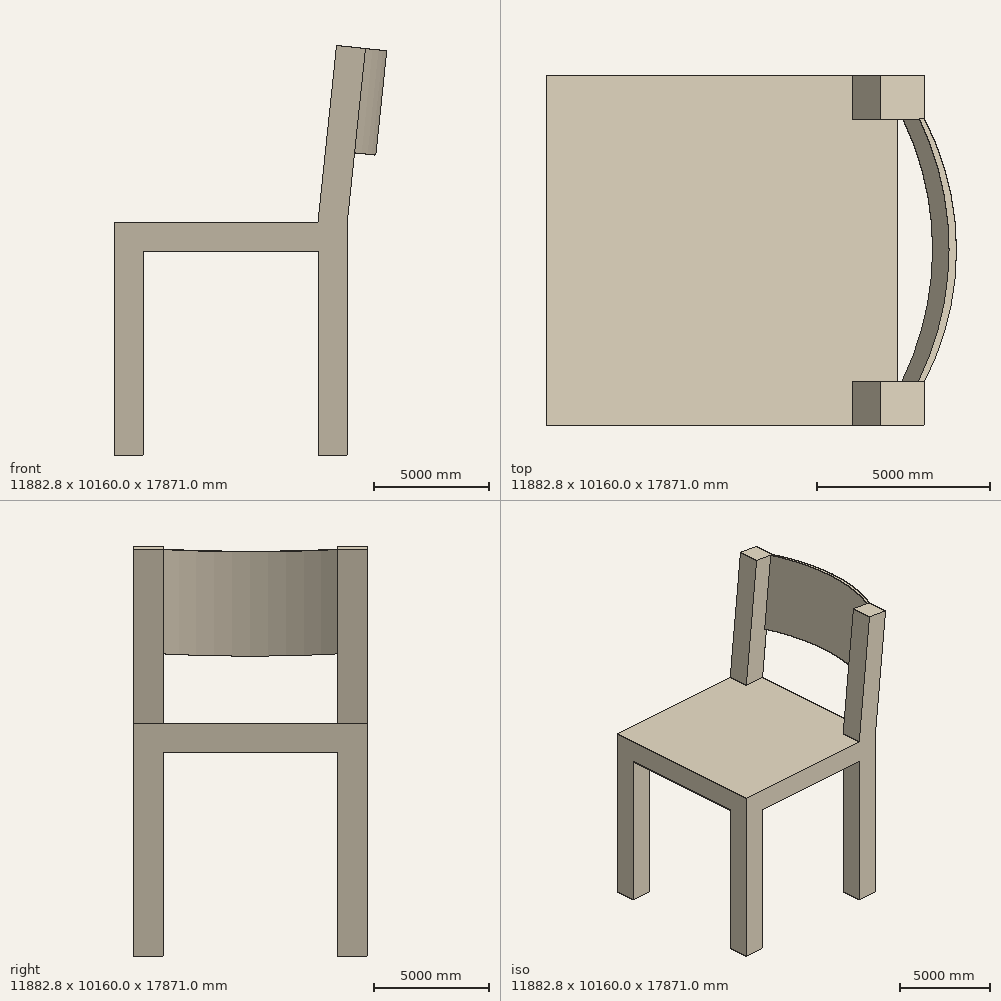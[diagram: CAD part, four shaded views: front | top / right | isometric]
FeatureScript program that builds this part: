
annotation { "Feature Type Name" : "Feature", "Feature Type Description" : "" }
export const myFeature = defineFeature(function(context is Context, id is Id, definition is map)
    precondition{}
    {
        {
            var Q0;
            Q0=qCreatedBy(makeId("Front.planeOp"),FACE);
            var sketch = newSketch(context, id + "F0", { "sketchPlane" : qUnion([Q0])});
            skLineSegment(sketch, "E0.bottom", {"start": v(-3222, -5083.92) * mm, "end": v(6938, -5083.92) * mm});
            skLineSegment(sketch, "E0.top", {"start": v(-3222, 5076.08) * mm, "end": v(6938, 5076.08) * mm});
            skLineSegment(sketch, "E0.left", {"start": v(-3222, -5083.92) * mm, "end": v(-3222, 5076.08) * mm});
            skLineSegment(sketch, "E0.right", {"start": v(6938, -5083.92) * mm, "end": v(6938, 5076.08) * mm});
            skSolve(sketch);
        }
        {
            var Q0;
            Q0=makeQuery(id+"F0.imprint","IMPRINT",FACE,{"disambiguationData":[TD([[makeQuery(id+"F0.imprint","IMPRINT",EDGE,{"derivedFrom":sQuery(id+"F0.wireOp",EDGE,"E0.bottom")}),1.0]])]});
            extrude(context, id + "F1", {"entities" : qUnion([Q0]), "depth" : 10160 * mm, "offsetDistance" : 25.4 * mm});
        }
        {
            var Q0;
            Q0=makeQuery(id+"F1.opExtrude","CAP_FACE",FACE,{"disambiguationData":[OSD([sQuery(id+"F0.wireOp",EDGE,"E0.bottom"),sQuery(id+"F0.wireOp",EDGE,"E0.top"),sQuery(id+"F0.wireOp",EDGE,"E0.left"),sQuery(id+"F0.wireOp",EDGE,"E0.right")])],"isStart":false});
            var sketch = newSketch(context, id + "F2", { "sketchPlane" : qUnion([Q0])});
            skLineSegment(sketch, "E1.bottom", {"start": v(5668, 3806.08) * mm, "end": v(-1952, 3806.08) * mm});
            skLineSegment(sketch, "E1.top", {"start": v(5668, -5083.92) * mm, "end": v(-1952, -5083.92) * mm});
            skLineSegment(sketch, "E1.left", {"start": v(5668, 3806.08) * mm, "end": v(5668, -5083.92) * mm});
            skLineSegment(sketch, "E1.right", {"start": v(-1952, 3806.08) * mm, "end": v(-1952, -5083.92) * mm});
            skSolve(sketch);
        }
        {
            var Q0;
            Q0 = qSketchRegion(id + "F2", true);
            extrude(context, id + "F3", {"entities" : qUnion([Q0]), "operationType" : NewBodyOperationType.REMOVE, "endBound" : BoundingType.THROUGH_ALL, "oppositeDirection" : true, "depth" : 10414 * mm, "offsetDistance" : 25.4 * mm});
        }
        {
            var Q0;
            Q0=makeQuery(id+"F1.opExtrude","SWEPT_FACE",FACE,{"disambiguationData":[OSD([sQuery(id+"F0.wireOp",EDGE,"E0.left")])]});
            var sketch = newSketch(context, id + "F4", { "sketchPlane" : qUnion([Q0])});
            skLineSegment(sketch, "E2.bottom", {"start": v(1270, 3806.08) * mm, "end": v(8890, 3806.08) * mm});
            skLineSegment(sketch, "E2.top", {"start": v(1270, -5083.92) * mm, "end": v(8890, -5083.92) * mm});
            skLineSegment(sketch, "E2.left", {"start": v(1270, 3806.08) * mm, "end": v(1270, -5083.92) * mm});
            skLineSegment(sketch, "E2.right", {"start": v(8890, 3806.08) * mm, "end": v(8890, -5083.92) * mm});
            skSolve(sketch);
        }
        {
            var Q0;
            Q0 = qSketchRegion(id + "F4", true);
            extrude(context, id + "F5", {"entities" : qUnion([Q0]), "operationType" : NewBodyOperationType.REMOVE, "endBound" : BoundingType.THROUGH_ALL, "oppositeDirection" : true, "depth" : 25.4 * mm, "offsetDistance" : 25.4 * mm});
        }
        {
            var Q0;
            Q0=makeQuery(id+"F1.opExtrude","SWEPT_FACE",FACE,{"disambiguationData":[OSD([sQuery(id+"F0.wireOp",EDGE,"E0.top")])]});
            var Q1;
            Q1=makeQuery(id+"F1.opExtrude","CAP_VERTEX",VERTEX,{"disambiguationData":[OSD([sQuery(id+"F0.wireOp",EDGE,"E0.top"),sQuery(id+"F0.wireOp",EDGE,"E0.left")])],"isStart":true});
            cPlane(context, id + "F6", {"entities" : qUnion([Q0, Q1]), "cplaneType" : CPlaneType.PLANE_POINT, "offset" : 25.4 * mm, "width" : 152.4 * mm, "height" : 152.4 * mm});
        }
        {
            var Q0;
            Q0=makeQuery(id+"F1.opExtrude","SWEPT_FACE",FACE,{"disambiguationData":[OSD([sQuery(id+"F0.wireOp",EDGE,"E0.right")])]});
            var Q1;
            Q1=makeQuery(id+"F1.opExtrude","CAP_VERTEX",VERTEX,{"disambiguationData":[OSD([sQuery(id+"F0.wireOp",EDGE,"E0.top"),sQuery(id+"F0.wireOp",EDGE,"E0.right")])],"isStart":false});
            cPlane(context, id + "F7", {"entities" : qUnion([Q0, Q1]), "cplaneType" : CPlaneType.PLANE_POINT, "offset" : 25.4 * mm, "width" : 152.4 * mm, "height" : 152.4 * mm});
        }
        {
            var Q0;
            Q0=makeQuery(id+"F1.opExtrude","SWEPT_EDGE",EDGE,{"disambiguationData":[OSD([sQuery(id+"F0.wireOp",EDGE,"E0.top"),sQuery(id+"F0.wireOp",EDGE,"E0.right")])]});
            var Q1;
            Q1=qCreatedBy(id+"F7.planeOp",FACE);
            cPlane(context, id + "F8", {"entities" : qUnion([Q0, Q1]), "cplaneType" : CPlaneType.LINE_ANGLE, "offset" : 25.4 * mm, "angle" : 6 * degree, "width" : 152.4 * mm, "height" : 152.4 * mm});
        }
        {
            var Q0;
            Q0=qCreatedBy(id+"F8.planeOp",FACE);
            var sketch = newSketch(context, id + "F9", { "sketchPlane" : qUnion([Q0])});
            skLineSegment(sketch, "E3.bottom", {"start": v(0, 13393.5) * mm, "end": v(10160, 13393.5) * mm});
            skLineSegment(sketch, "E3.top", {"start": v(0, 5773.5) * mm, "end": v(10160, 5773.5) * mm});
            skLineSegment(sketch, "E3.left", {"start": v(0, 13393.5) * mm, "end": v(0, 5773.5) * mm});
            skLineSegment(sketch, "E3.right", {"start": v(10160, 13393.5) * mm, "end": v(10160, 5773.5) * mm});
            skSolve(sketch);
        }
        {
            var Q0;
            Q0 = qSketchRegion(id + "F9", true);
            extrude(context, id + "F10", {"entities" : qUnion([Q0]), "depth" : 1270 * mm, "offsetDistance" : 25.4 * mm});
        }
        {
            var Q0;
            Q0=makeQuery(id+"F10.opExtrude","CAP_FACE",FACE,{"disambiguationData":[OSD([sQuery(id+"F9.wireOp",EDGE,"E3.bottom"),sQuery(id+"F9.wireOp",EDGE,"E3.top"),sQuery(id+"F9.wireOp",EDGE,"E3.left"),sQuery(id+"F9.wireOp",EDGE,"E3.right")])],"isStart":false});
            var sketch = newSketch(context, id + "F11", { "sketchPlane" : qUnion([Q0])});
            skLineSegment(sketch, "E4.bottom", {"start": v(1270, 13393.5) * mm, "end": v(8890, 13393.5) * mm});
            skLineSegment(sketch, "E4.top", {"start": v(1270, 5773.5) * mm, "end": v(8890, 5773.5) * mm});
            skLineSegment(sketch, "E4.left", {"start": v(1270, 13393.5) * mm, "end": v(1270, 5773.5) * mm});
            skLineSegment(sketch, "E4.right", {"start": v(8890, 13393.5) * mm, "end": v(8890, 5773.5) * mm});
            skSolve(sketch);
        }
        {
            var Q0;
            Q0 = qSketchRegion(id + "F11", true);
            extrude(context, id + "F12", {"entities" : qUnion([Q0]), "operationType" : NewBodyOperationType.REMOVE, "endBound" : BoundingType.THROUGH_ALL, "oppositeDirection" : true, "depth" : 25.4 * mm, "offsetDistance" : 25.4 * mm});
        }
        {
            var Q0;
            {var subQ1=sQuery(id+"F9.wireOp",EDGE,"E3.left");var subQ3=sQuery(id+"F9.wireOp",EDGE,"E3.bottom");Q0=makeQuery(id+"F12.boolean.opBoolean","SPLIT",FACE,{"disambiguationData":[TD([makeQuery(id+"F10.opExtrude","SWEPT_FACE",FACE,{"disambiguationData":[OSD([subQ1])]})])],"derivedFrom":makeQuery(id+"F10.opExtrude","SWEPT_FACE",FACE,{"disambiguationData":[OSD([subQ3])]})});}
            var Q1;
            {var subQ0=sQuery(id+"F9.wireOp",EDGE,"E3.right");var subQ3=sQuery(id+"F9.wireOp",EDGE,"E3.bottom");Q1=makeQuery(id+"F12.boolean.opBoolean","SPLIT",FACE,{"disambiguationData":[TD([makeQuery(id+"F10.opExtrude","SWEPT_FACE",FACE,{"disambiguationData":[OSD([subQ0])]})])],"derivedFrom":makeQuery(id+"F10.opExtrude","SWEPT_FACE",FACE,{"disambiguationData":[OSD([subQ3])]})});}
            cPlane(context, id + "F13", {"entities" : qUnion([Q0, Q1]), "cplaneType" : CPlaneType.MID_PLANE, "offset" : 25.4 * mm, "width" : 152.4 * mm, "height" : 152.4 * mm});
        }
        {
            var Q0;
            Q0=qCreatedBy(id+"F13.planeOp",FACE);
            var sketch = newSketch(context, id + "F14", { "sketchPlane" : qUnion([Q0])});
            skArc(sketch, "E5", {"start": v(6369.4, -8890) * mm, "mid": v(7300.77, -5080) * mm, "end": v(6369.4, -1270) * mm});
            skLineSegment(sketch, "E6", {"start": v(6369.4, -8890) * mm, "end": v(6186.82, -8890) * mm});
            skArc(sketch, "E7", {"start": v(6186.82, -8890) * mm, "mid": v(7084.34, -5077.24) * mm, "end": v(6212.09, -1258.61) * mm});
            skLineSegment(sketch, "E8", {"start": v(6212.09, -1258.61) * mm, "end": v(6369.4, -1270) * mm});
            skSolve(sketch);
        }
        {
            var Q0;
            Q0 = qSketchRegion(id + "F14", true);
            extrude(context, id + "F15", {"entities" : qUnion([Q0]), "oppositeDirection" : true, "depth" : 4572 * mm, "offsetDistance" : 25.4 * mm});
        }
        {
            var Q0;
            {var subQ1=sQuery(id+"F9.wireOp",EDGE,"E3.left");var subQ2=sQuery(id+"F9.wireOp",EDGE,"E3.top");Q0=makeQuery(id+"F12.boolean.opBoolean","SPLIT",FACE,{"disambiguationData":[TD([makeQuery(id+"F10.opExtrude","SWEPT_FACE",FACE,{"disambiguationData":[OSD([subQ1])]})])],"derivedFrom":makeQuery(id+"F10.opExtrude","SWEPT_FACE",FACE,{"disambiguationData":[OSD([subQ2])]})});}
            var sketch = newSketch(context, id + "F16", { "sketchPlane" : qUnion([Q0])});
            skSolve(sketch);
        }
        {
            var Q0;
            {var subQ0=sQuery(id+"F9.wireOp",EDGE,"E3.left");var subQ1=sQuery(id+"F9.wireOp",EDGE,"E3.top");Q0=makeQuery(id+"F16.imprint","IMPRINT",FACE,{"disambiguationData":[TD([[makeQuery(id+"F16.imprint","IMPRINT",EDGE,{"derivedFrom":makeQuery(id+"F10.opExtrude","SWEPT_EDGE",EDGE,{"disambiguationData":[OSD([subQ1,subQ0])]})}),1.0]])]});}
            extrude(context, id + "F17", {"entities" : qUnion([Q0]), "operationType" : NewBodyOperationType.ADD, "endBound" : BoundingType.UP_TO_NEXT, "depth" : 25.4 * mm, "offsetDistance" : 25.4 * mm});
        }
        {
            var Q0;
            {var subQ0=sQuery(id+"F9.wireOp",EDGE,"E3.right");var subQ2=sQuery(id+"F9.wireOp",EDGE,"E3.top");Q0=makeQuery(id+"F12.boolean.opBoolean","SPLIT",FACE,{"disambiguationData":[TD([makeQuery(id+"F10.opExtrude","SWEPT_FACE",FACE,{"disambiguationData":[OSD([subQ0])]})])],"derivedFrom":makeQuery(id+"F10.opExtrude","SWEPT_FACE",FACE,{"disambiguationData":[OSD([subQ2])]})});}
            extrude(context, id + "F18", {"entities" : qUnion([Q0]), "operationType" : NewBodyOperationType.ADD, "endBound" : BoundingType.UP_TO_NEXT, "depth" : 25.4 * mm, "offsetDistance" : 25.4 * mm});
        }
    });
